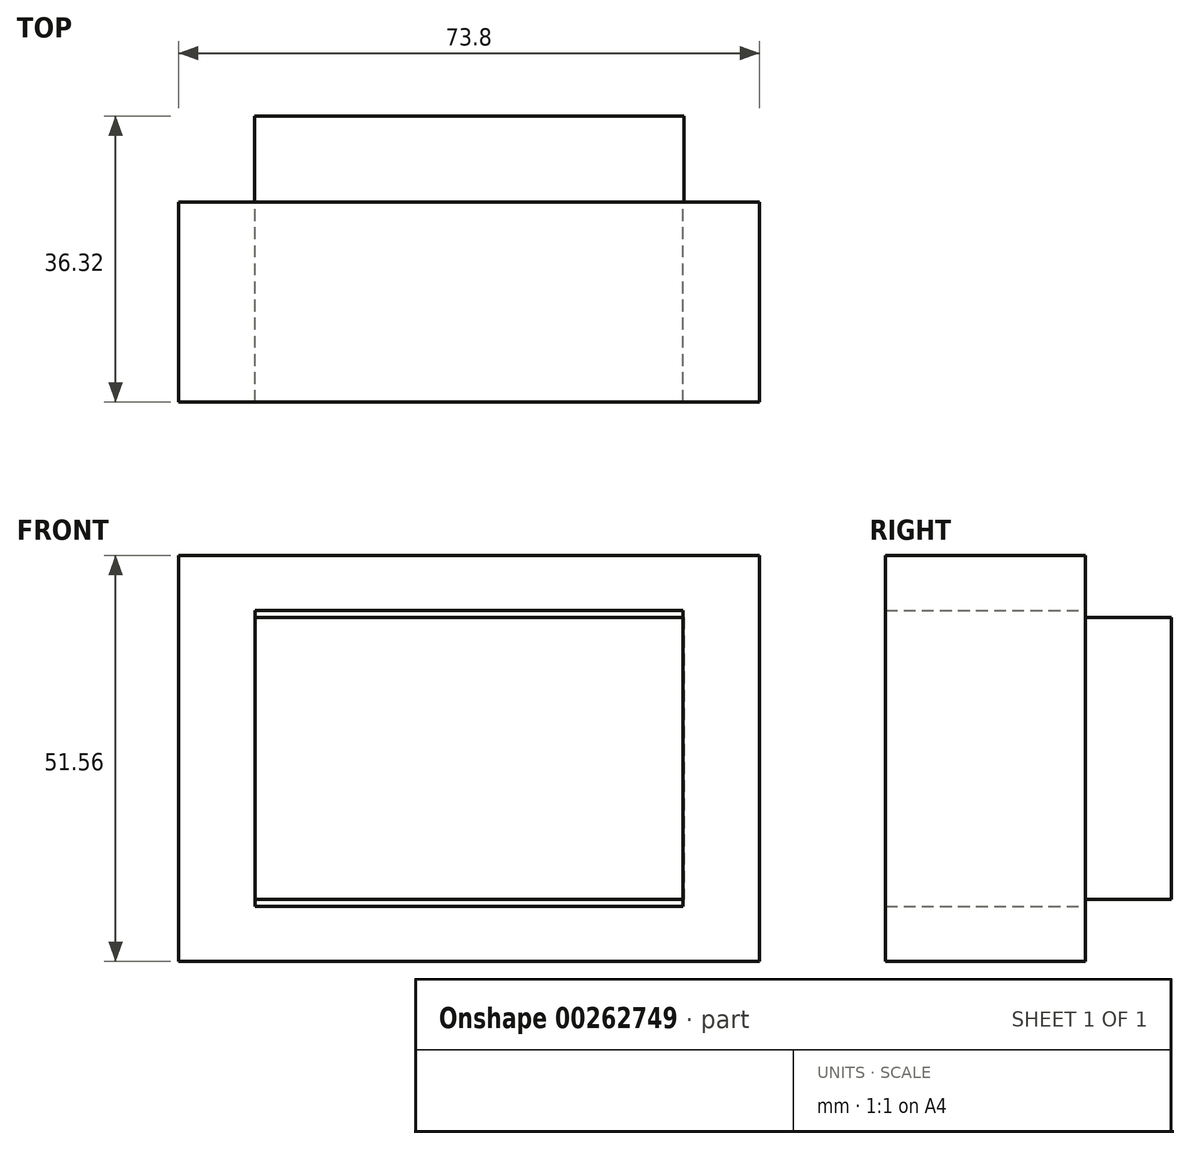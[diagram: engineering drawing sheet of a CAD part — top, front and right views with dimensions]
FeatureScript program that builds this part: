
annotation { "Feature Type Name" : "Feature", "Feature Type Description" : "" }
export const myFeature = defineFeature(function(context is Context, id is Id, definition is map)
    precondition{}
    {
        {
            var Q0;
            Q0=qCreatedBy(makeId("Front.planeOp"),FACE);
            var sketch = newSketch(context, id + "F0", { "sketchPlane" : qUnion([Q0])});
            skLineSegment(sketch, "E0.bottom", {"start": v(-36.9, 25.78) * mm, "end": v(36.9, 25.78) * mm});
            skLineSegment(sketch, "E0.top", {"start": v(-36.9, -25.78) * mm, "end": v(36.9, -25.78) * mm});
            skLineSegment(sketch, "E0.left", {"start": v(-36.9, 25.78) * mm, "end": v(-36.9, -25.78) * mm});
            skLineSegment(sketch, "E0.right", {"start": v(36.9, 25.78) * mm, "end": v(36.9, -25.78) * mm});
            skPoint(sketch, "E0.middle", {"position": v(0, 0) * mm});
            skLineSegment(sketch, "E1.bottom", {"start": v(-27.19, 18.81) * mm, "end": v(27.19, 18.81) * mm});
            skLineSegment(sketch, "E1.top", {"start": v(-27.19, -18.81) * mm, "end": v(27.19, -18.81) * mm});
            skLineSegment(sketch, "E1.left", {"start": v(-27.19, 18.81) * mm, "end": v(-27.19, -18.81) * mm});
            skLineSegment(sketch, "E1.right", {"start": v(27.19, 18.81) * mm, "end": v(27.19, -18.81) * mm});
            skLineSegment(sketch, "E2", {"start": v(27.19, 18.81) * mm, "end": v(36.9, 25.78) * mm});
            skLineSegment(sketch, "E3", {"start": v(-27.19, 18.81) * mm, "end": v(-36.9, 25.78) * mm});
            skLineSegment(sketch, "E4", {"start": v(27.19, -18.81) * mm, "end": v(36.9, -25.78) * mm});
            skLineSegment(sketch, "E5", {"start": v(-27.19, -18.81) * mm, "end": v(-36.9, -25.78) * mm});
            skSolve(sketch);
        }
        {
            var Q0;
            Q0=qCreatedBy(makeId("Front.planeOp"),FACE);
            var sketch = newSketch(context, id + "F1", { "sketchPlane" : qUnion([Q0])});
            skLineSegment(sketch, "E6.bottom", {"start": v(-27.29, 17.93) * mm, "end": v(27.29, 17.93) * mm});
            skLineSegment(sketch, "E6.top", {"start": v(-27.29, -17.93) * mm, "end": v(27.29, -17.93) * mm});
            skLineSegment(sketch, "E6.left", {"start": v(-27.29, 17.93) * mm, "end": v(-27.29, -17.93) * mm});
            skLineSegment(sketch, "E6.right", {"start": v(27.29, 17.93) * mm, "end": v(27.29, -17.93) * mm});
            skPoint(sketch, "E6.middle", {"position": v(0, 0) * mm});
            skSolve(sketch);
        }
        {
            var Q0;
            Q0 = qSketchRegion(id + "F0", true);
            extrude(context, id + "F2", {"entities" : qUnion([Q0]), "depth" : 25.4 * mm});
        }
        {
            var Q0;
            Q0 = qSketchRegion(id + "F1", true);
            extrude(context, id + "F3", {"entities" : qUnion([Q0]), "operationType" : NewBodyOperationType.ADD, "oppositeDirection" : true, "depth" : 10.92 * mm});
        }
    });
